# Revit family: KingswayGroup_HtchSstms_ClinicRoomHatchWithVisionPanel
name_source: partatom
category: Specialty Equipment
units: mm (PartAtom-declared; Revit-internal decimal feet)

## family parameters
Always vertical = No
Cut with Voids When Loaded = No
Part Type = Normal
Room Calculation Point = No
Round Connector Dimension = Use Diameter
Shared = No
Work Plane-Based = No

## types (2) — shared parameters
AssetType = Fixed
BIMObjectName = KingswayGroup_HatchSystems_ClinicRoomHatchWithVisionPanel
Category = Ss_25_30_20_35:Hatch systems
Color = For full range of available finishes and colours, contact Kingsway Group
DurationUnit = year
Features = A secure door hatch with Vision Panel to provide a safe serving solution with the added benefit of observation capabilities. The hatch allows for communication or for items to be passed out of a secure room without needing to open the door leaf to increase staff safety in high risk areas. It is flush to the patient side with no visible fixings and can be fitted with a folding serving shelf to the staff side.
Finish = For full range of available finishes and colours, contact Kingsway Group
HatchMaterial = NBS_Concept
Manufacturer = Kingsway Group
ManufacturerName = Kingsway Group
ManufacturerURL = https://kingswaygroupglobal.com
Material = For full range of available material, contact Kingsway Group
ModelReference = Clinic Room Hatch With Vision Panel
NominalHeight = 846 mm  [stored 2.77559 ft]
NominalLength = 584 mm  [stored 1.91601 ft]
PlateMaterial = NBS_Concept
ProductInformation = https://kingswaygroupglobal.com
URL = https://kingswaygroupglobal.com
Uniclass2015Code = Ss_25_30_20_35
Uniclass2015Title = Hatch systems
Uniclass2015Version = Products v1.36
Version = 1
VisionPanelMaterial = NBS_Concept
WarrantyDescription = 5-Year Guarantee *For faulty manufacture and not for damage
WarrantyDurationParts = 5
WarrantyDurationUnit = year
zero-valued in all types: Default Elevation

## per-type parameters (varying)
| type | Description | DoorThickness | DoorThickness44mm | DoorThickness54mm | Model | ModelNumber | Name | NominalWidth | Size |
| KG172 Door Hatch for 54mm Door | Anti-Ligature Secure Observation Door Hatch for 54mm Door | 54 mm  [stored 0.177165 ft] | No | Yes | KG172 | KG172 | HatchSystems_ClinicRoomHatchWithVisionPanel_KG172_KingswayGroup | 54 mm  [stored 0.177165 ft] | 584 x 846 x 54 mm |
| KG171 Door Hatch for 44mm Door | Anti-Ligature Secure Observation Door Hatch for 44mm Door | 44 mm  [stored 0.144357 ft] | Yes | No | KG171 | KG171 | HatchSystems_ClinicRoomHatchWithVisionPanel_KG171_KingswayGroup | 44 mm  [stored 0.144357 ft] | 584 x 846 x 44 mm |

note: [stored X ft] marks values corroborated as IEEE doubles in the binary element streams (Revit-internal decimal feet)

## geometry (parser evidence)
native form markers: Sweep x2
no freeform markers — native parametric forms only
